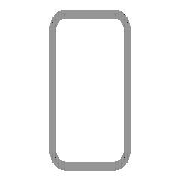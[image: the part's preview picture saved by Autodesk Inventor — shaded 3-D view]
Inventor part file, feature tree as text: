
AUTODESK INVENTOR PART (.ipt)
format: ipt  version: 2025 (Build 290162010, 162A)  size: 133,632 bytes
history: native  units: mm (DEFAULTED — no unit token found)
features: other x4, sketch x1, plane x1
ambient origin geometry x8: Origin, YZ Plane, XZ Plane, XY Plane, X Axis, Y Axis, Z Axis, Center Point
bodies: Solid1 (feature_tree), Body (feature_tree)
feature tree (6):
  parser-record x1  (decoder bookkeeping rows leaked as tree rows — omitted from the tree; the rows remain in map.json)
  other  "Driven Length"
  other  "Start Plane"
  other  "End Plane"
  sketch  "Sketch3"  dims[d3=1420.0mm d4=0.0mm d7=6.0mm d9=40.0mm d11=60.0mm d12=3.0mm d13=40.0mm d14=1460.0mm d15=20.0mm d16=30.0mm d17=90.0deg d18=1420.0mm]
  plane  "Work Plane3"
